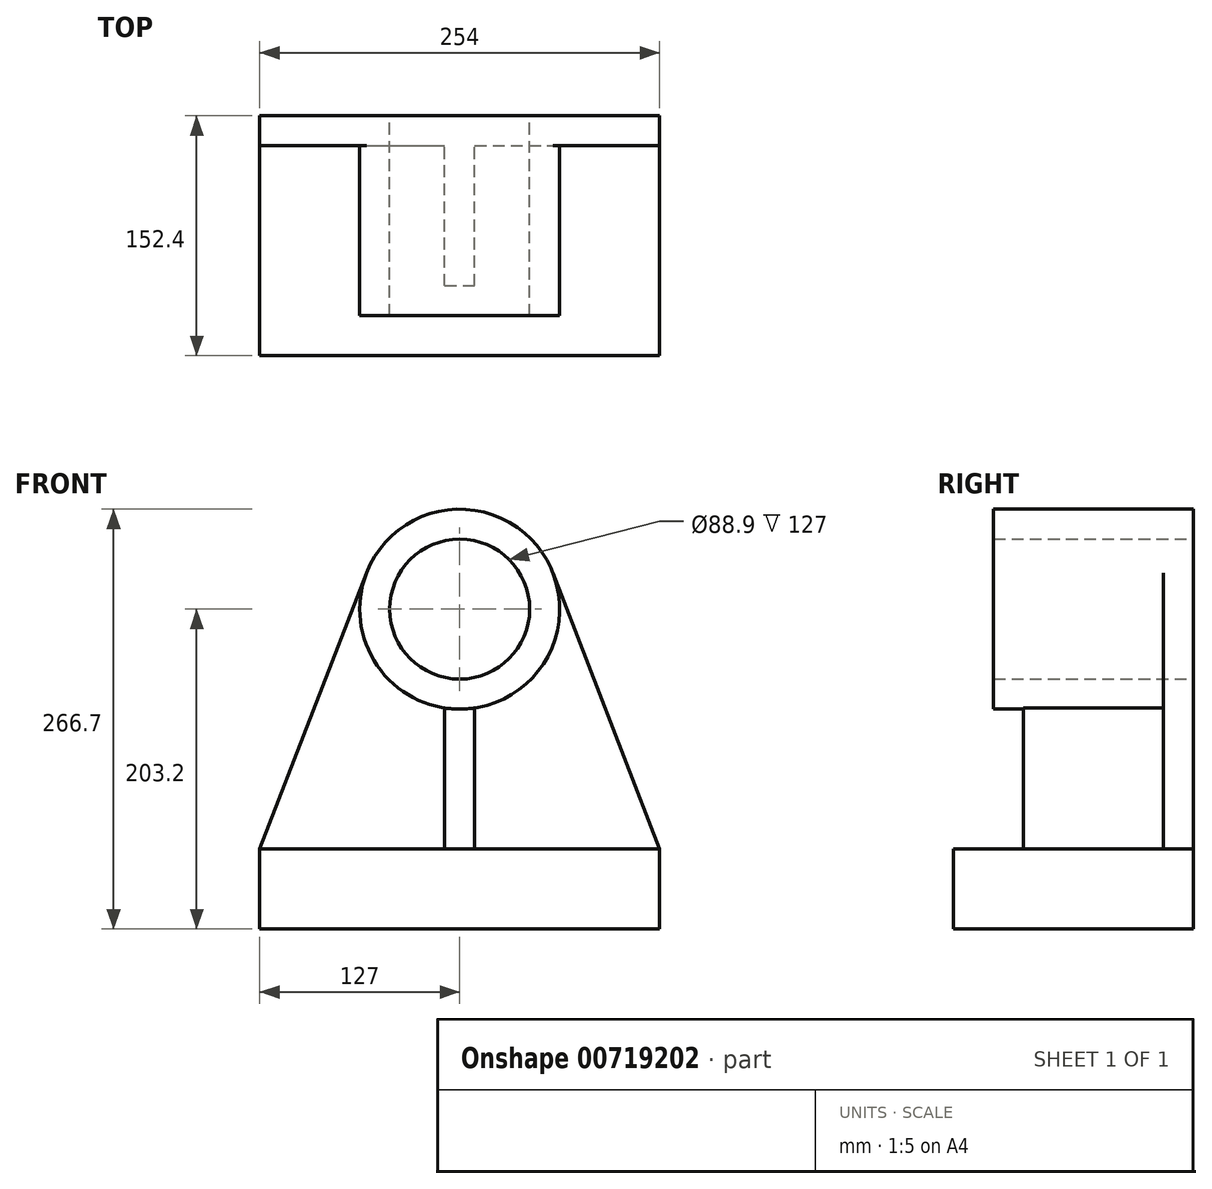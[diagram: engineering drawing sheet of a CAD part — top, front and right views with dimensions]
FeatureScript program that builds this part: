
annotation { "Feature Type Name" : "Feature", "Feature Type Description" : "" }
export const myFeature = defineFeature(function(context is Context, id is Id, definition is map)
    precondition{}
    {
        {
            var Q0;
            Q0=qCreatedBy(makeId("Front.planeOp"),FACE);
            var sketch = newSketch(context, id + "F0", { "sketchPlane" : qUnion([Q0])});
            skLineSegment(sketch, "E0", {"start": v(0, 0) * mm, "end": v(0, 50.8) * mm});
            skLineSegment(sketch, "E1", {"start": v(0, 50.8) * mm, "end": v(254, 50.8) * mm});
            skLineSegment(sketch, "E2", {"start": v(254, 50.8) * mm, "end": v(254, 0) * mm});
            skLineSegment(sketch, "E3", {"start": v(254, 0) * mm, "end": v(0, 0) * mm});
            skLineSegment(sketch, "E4", {"start": v(0, 50.8) * mm, "end": v(67.77, 226.1) * mm});
            skLineSegment(sketch, "E5", {"start": v(254, 50.8) * mm, "end": v(186.23, 226.1) * mm});
            skCircle(sketch, "E6", {"center": v(127, 203.2) * mm, "radius": 63.5 * mm});
            skCircle(sketch, "E7", {"center": v(127, 203.2) * mm, "radius": 44.45 * mm});
            skLineSegment(sketch, "E8", {"start": v(117.47, 50.8) * mm, "end": v(117.47, 140.42) * mm});
            skLineSegment(sketch, "E9", {"start": v(136.53, 50.8) * mm, "end": v(136.53, 140.42) * mm});
            skLineSegment(sketch, "E10", {"start": v(127, 247.65) * mm, "end": v(127, 8.1) * mm, "construction": true});
            skSolve(sketch);
        }
        {
            var Q0;
            Q0=makeQuery(id+"F0.imprint","IMPRINT",FACE,{"disambiguationData":[TD([[makeQuery(id+"F0.imprint","IMPRINT",EDGE,{"derivedFrom":sQuery(id+"F0.wireOp",EDGE,"E7")}),-1.0]])]});
            extrude(context, id + "F1", {"entities" : qUnion([Q0]), "depth" : 127 * mm, "offsetDistance" : 25.4 * mm});
        }
        {
            var Q0;
            {var subQ0=sQuery(id+"F0.wireOp",EDGE,"E5");Q0=makeQuery(id+"F0.imprint","IMPRINT",FACE,{"disambiguationData":[TD([[makeQuery(id+"F0.imprint","IMPRINT",EDGE,{"derivedFrom":subQ0}),1.0]])]});}
            var Q1;
            {var subQ0=sQuery(id+"F0.wireOp",EDGE,"E4");Q1=makeQuery(id+"F0.imprint","IMPRINT",FACE,{"disambiguationData":[TD([[makeQuery(id+"F0.imprint","IMPRINT",EDGE,{"derivedFrom":subQ0}),-1.0]])]});}
            extrude(context, id + "F2", {"entities" : qUnion([Q0, Q1]), "operationType" : NewBodyOperationType.ADD, "depth" : 19.05 * mm, "offsetDistance" : 25.4 * mm});
        }
        {
            var Q0;
            {var subQ0=sQuery(id+"F0.wireOp",EDGE,"E8");Q0=makeQuery(id+"F0.imprint","IMPRINT",FACE,{"disambiguationData":[TD([[makeQuery(id+"F0.imprint","IMPRINT",EDGE,{"derivedFrom":subQ0}),-1.0]])]});}
            extrude(context, id + "F3", {"entities" : qUnion([Q0]), "operationType" : NewBodyOperationType.ADD, "depth" : 107.95 * mm, "offsetDistance" : 25.4 * mm});
        }
        {
            var Q0;
            {var subQ4=sQuery(id+"F0.wireOp",EDGE,"E0");Q0=makeQuery(id+"F0.imprint","IMPRINT",FACE,{"disambiguationData":[TD([[makeQuery(id+"F0.imprint","IMPRINT",EDGE,{"derivedFrom":subQ4}),-1.0]])]});}
            extrude(context, id + "F4", {"entities" : qUnion([Q0]), "operationType" : NewBodyOperationType.ADD, "depth" : 152.4 * mm, "offsetDistance" : 25.4 * mm});
        }
        {
            var Q0;
            Q0=makeQuery(id+"F0.imprint","IMPRINT",FACE,{"disambiguationData":[TD([[makeQuery(id+"F0.imprint","IMPRINT",EDGE,{"derivedFrom":sQuery(id+"F0.wireOp",EDGE,"E7")}),-1.0]])]});
            var Q1;
            {var subQ4=sQuery(id+"F0.wireOp",EDGE,"E0");Q1=makeQuery(id+"F0.imprint","IMPRINT",FACE,{"disambiguationData":[TD([[makeQuery(id+"F0.imprint","IMPRINT",EDGE,{"derivedFrom":subQ4}),-1.0]])]});}
            extrude(context, id + "F5", {"entities" : qUnion([Q0, Q1]), "operationType" : NewBodyOperationType.ADD, "depth" : 25.4 * mm, "offsetDistance" : 25.4 * mm});
        }
    });
